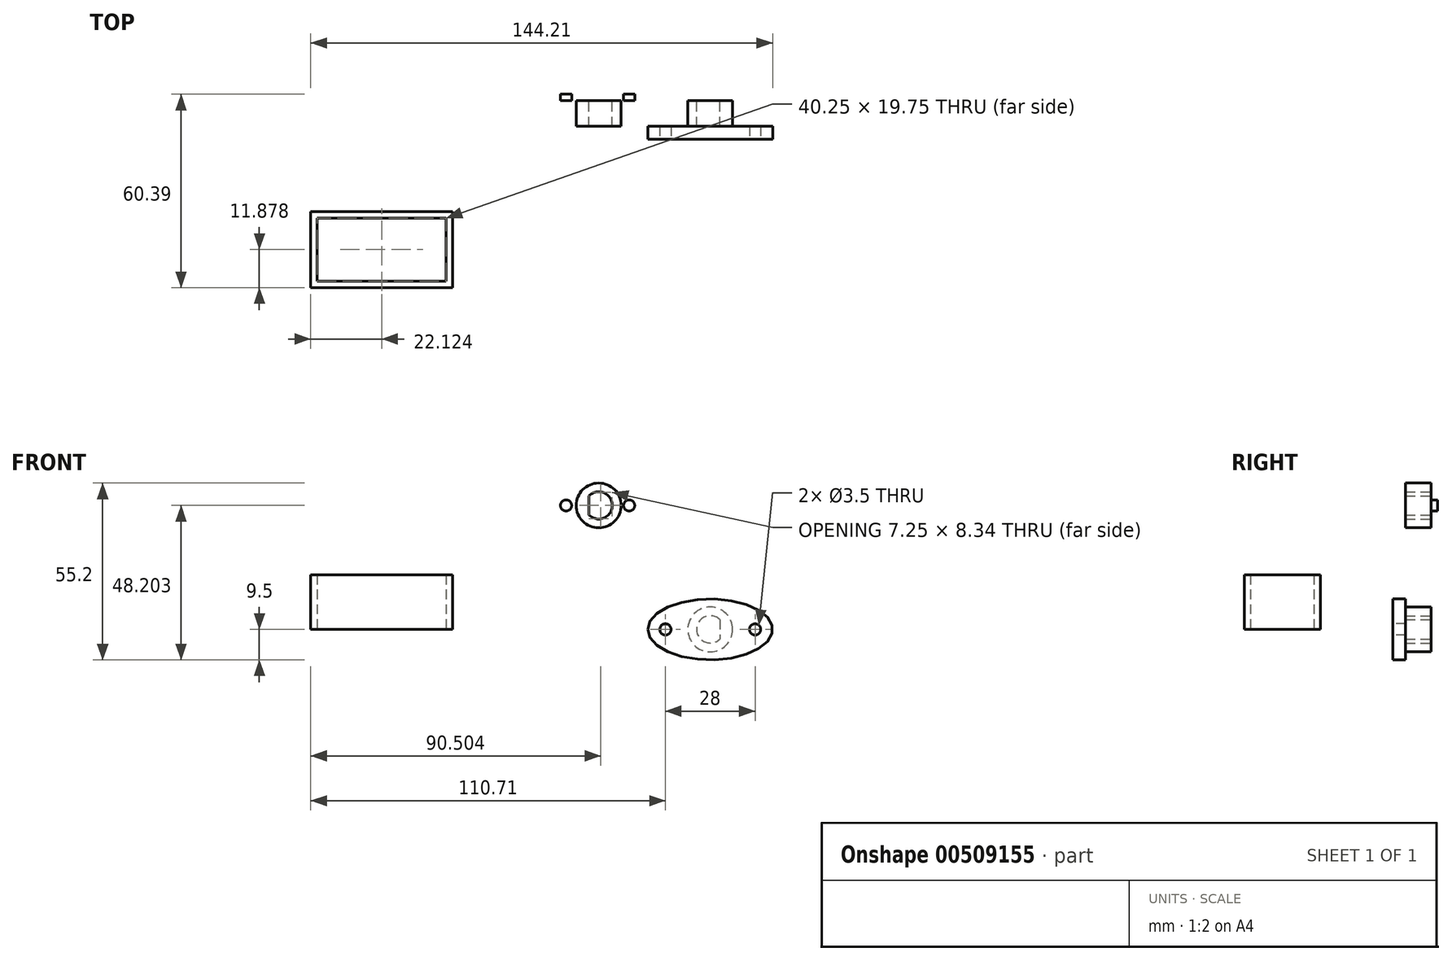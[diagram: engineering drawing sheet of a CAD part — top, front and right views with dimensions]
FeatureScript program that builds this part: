
annotation { "Feature Type Name" : "Feature", "Feature Type Description" : "" }
export const myFeature = defineFeature(function(context is Context, id is Id, definition is map)
    precondition{}
    {
        {
            var Q0;
            Q0=qCreatedBy(makeId("Front.planeOp"),FACE);
            var sketch = newSketch(context, id + "F0", { "sketchPlane" : qUnion([Q0])});
            skPoint(sketch, "E0.middle", {"position": v(0, 0) * mm});
            skCircle(sketch, "E1", {"center": v(0, 0) * mm, "radius": 7 * mm});
            skSolve(sketch);
        }
        {
            var Q0;
            Q0=makeQuery(id+"F0.imprint","IMPRINT",FACE,{"disambiguationData":[TD([[makeQuery(id+"F0.imprint","IMPRINT",EDGE,{"derivedFrom":sQuery(id+"F0.wireOp",EDGE,"E1")}),1.0]])]});
            extrude(context, id + "F1", {"entities" : qUnion([Q0]), "depth" : 8 * mm, "offsetDistance" : 25 * mm});
        }
        {
            var Q0;
            Q0=makeQuery(id+"F1.opExtrude","CAP_FACE",FACE,{"disambiguationData":[OSD([sQuery(id+"F0.wireOp",EDGE,"E0.bottom"),sQuery(id+"F0.wireOp",EDGE,"E0.top"),sQuery(id+"F0.wireOp",EDGE,"E0.left"),sQuery(id+"F0.wireOp",EDGE,"E0.right"),sQuery(id+"F0.wireOp",EDGE,"E1")])],"isStart":false});
            var sketch = newSketch(context, id + "F2", { "sketchPlane" : qUnion([Q0])});
            skEllipse(sketch, "E2", {"center": v(0, 0) * mm, "majorRadius": 19.5 * mm, "minorRadius": 9.5 * mm, "majorAxis": v(-1, 0)});
            skSolve(sketch);
        }
        {
            var Q0;
            Q0 = qSketchRegion(id + "F2", true);
            extrude(context, id + "F3", {"entities" : qUnion([Q0]), "operationType" : NewBodyOperationType.ADD, "depth" : 4 * mm, "offsetDistance" : 25 * mm});
        }
        {
            var Q0;
            Q0=makeQuery(id+"F3.opExtrude","CAP_FACE",FACE,{"disambiguationData":[OSD([sQuery(id+"F2.wireOp",EDGE,"E2")])],"isStart":false});
            var sketch = newSketch(context, id + "F4", { "sketchPlane" : qUnion([Q0])});
            skCircle(sketch, "E3", {"center": v(-14, 0) * mm, "radius": 1.75 * mm});
            skCircle(sketch, "E4", {"center": v(14, 0) * mm, "radius": 1.75 * mm});
            skSolve(sketch);
        }
        {
            var Q0;
            Q0 = qSketchRegion(id + "F4", true);
            extrude(context, id + "F5", {"entities" : qUnion([Q0]), "operationType" : NewBodyOperationType.REMOVE, "oppositeDirection" : true, "depth" : 4 * mm, "offsetDistance" : 25 * mm});
        }
        {
            var Q0;
            Q0=makeQuery(id+"F1.opExtrude","CAP_FACE",FACE,{"disambiguationData":[OSD([sQuery(id+"F0.wireOp",EDGE,"E1")])],"isStart":true});
            var sketch = newSketch(context, id + "F6", { "sketchPlane" : qUnion([Q0])});
            skCircle(sketch, "E5", {"center": v(0, 0) * mm, "radius": 4.25 * mm});
            skLineSegment(sketch, "E6", {"start": v(0, 0) * mm, "end": v(-3, 0) * mm});
            skLineSegment(sketch, "E7", {"start": v(-3, 3.01) * mm, "end": v(-3, -3.01) * mm});
            skSolve(sketch);
        }
        {
            var Q0;
            {var subQ0=sQuery(id+"F6.wireOp",EDGE,"E7");var subQ4=makeQuery(id+"F6.imprint","IMPRINT",VERTEX,{"derivedFrom":subQ0});Q0=makeQuery(id+"F6.imprint","IMPRINT",FACE,{"disambiguationData":[TD([[makeQuery(id+"F6.imprint","IMPRINT",EDGE,{"disambiguationData":[TD([[subQ4,1.0]])],"derivedFrom":subQ0}),1.0]])]});}
            extrude(context, id + "F7", {"entities" : qUnion([Q0]), "operationType" : NewBodyOperationType.REMOVE, "oppositeDirection" : true, "depth" : 8 * mm, "offsetDistance" : 25 * mm});
        }
        {
            var Q0;
            Q0=qCreatedBy(makeId("Top.planeOp"),FACE);
            var sketch = newSketch(context, id + "F8", { "sketchPlane" : qUnion([Q0])});
            skLineSegment(sketch, "E8.bottom", {"start": v(-122.71, -36.64) * mm, "end": v(-82.46, -36.64) * mm});
            skLineSegment(sketch, "E8.top", {"start": v(-122.71, -56.39) * mm, "end": v(-82.46, -56.39) * mm});
            skLineSegment(sketch, "E8.left", {"start": v(-122.71, -36.64) * mm, "end": v(-122.71, -56.39) * mm});
            skLineSegment(sketch, "E8.right", {"start": v(-82.46, -36.64) * mm, "end": v(-82.46, -56.39) * mm});
            skLineSegment(sketch, "E9.bottom", {"start": v(-124.71, -34.64) * mm, "end": v(-80.46, -34.64) * mm});
            skLineSegment(sketch, "E9.top", {"start": v(-124.71, -58.39) * mm, "end": v(-80.46, -58.39) * mm});
            skLineSegment(sketch, "E9.left", {"start": v(-124.71, -34.64) * mm, "end": v(-124.71, -58.39) * mm});
            skLineSegment(sketch, "E9.right", {"start": v(-80.46, -34.64) * mm, "end": v(-80.46, -58.39) * mm});
            skSolve(sketch);
        }
        {
            var Q0;
            Q0=makeQuery(id+"F8.imprint","IMPRINT",FACE,{"disambiguationData":[TD([[makeQuery(id+"F8.imprint","IMPRINT",EDGE,{"derivedFrom":sQuery(id+"F8.wireOp",EDGE,"E8.bottom")}),1.0]])]});
            extrude(context, id + "F9", {"entities" : qUnion([Q0]), "depth" : 17 * mm, "offsetDistance" : 25 * mm});
        }
        {
            var Q0;
            Q0=qCreatedBy(makeId("Front.planeOp"),FACE);
            var sketch = newSketch(context, id + "F10", { "sketchPlane" : qUnion([Q0])});
            skPoint(sketch, "E10.middle", {"position": v(-34.83, 38.7) * mm});
            skCircle(sketch, "E11", {"center": v(-34.83, 38.7) * mm, "radius": 7 * mm});
            skCircle(sketch, "E12", {"center": v(-34.83, 38.7) * mm, "radius": 4.25 * mm});
            skLineSegment(sketch, "E13", {"start": v(-34.83, 38.7) * mm, "end": v(-37.83, 38.7) * mm});
            skLineSegment(sketch, "E14", {"start": v(-37.83, 41.71) * mm, "end": v(-37.83, 35.7) * mm});
            skSolve(sketch);
        }
        {
            var Q0;
            Q0=makeQuery(id+"F10.imprint","IMPRINT",FACE,{"disambiguationData":[TD([[makeQuery(id+"F10.imprint","IMPRINT",EDGE,{"derivedFrom":sQuery(id+"F10.wireOp",EDGE,"E11")}),1.0]])]});
            var Q1;
            {var subQ0=sQuery(id+"F10.wireOp",EDGE,"E14");var subQ4=makeQuery(id+"F10.imprint","IMPRINT",VERTEX,{"derivedFrom":subQ0});Q1=makeQuery(id+"F10.imprint","IMPRINT",FACE,{"disambiguationData":[TD([[makeQuery(id+"F10.imprint","IMPRINT",EDGE,{"disambiguationData":[TD([[subQ4,1.0]])],"derivedFrom":subQ0}),-1.0]])]});}
            extrude(context, id + "F11", {"entities" : qUnion([Q0, Q1]), "depth" : 8 * mm, "offsetDistance" : 25 * mm});
        }
        {
            var Q0;
            Q0=makeQuery(id+"F11.opExtrude","CAP_FACE",FACE,{"disambiguationData":[OSD([sQuery(id+"F10.wireOp",EDGE,"E11"),sQuery(id+"F10.wireOp",EDGE,"E12"),sQuery(id+"F10.wireOp",EDGE,"E14")])],"isStart":true});
            var sketch = newSketch(context, id + "F12", { "sketchPlane" : qUnion([Q0])});
            skCircle(sketch, "E15", {"center": v(25.3, 38.7) * mm, "radius": 1.75 * mm});
            skPoint(sketch, "E15.centerSnap0", {"position": v(30.58, 38.7) * mm});
            skCircle(sketch, "E16", {"center": v(45, 38.7) * mm, "radius": 1.75 * mm});
            skPoint(sketch, "E16.centerSnap0", {"position": v(37.83, 38.7) * mm});
            skSolve(sketch);
        }
        {
            var Q0;
            Q0 = qSketchRegion(id + "F12", true);
            extrude(context, id + "F13", {"entities" : qUnion([Q0]), "operationType" : NewBodyOperationType.ADD, "depth" : 2 * mm, "offsetDistance" : 25 * mm});
        }
    });
